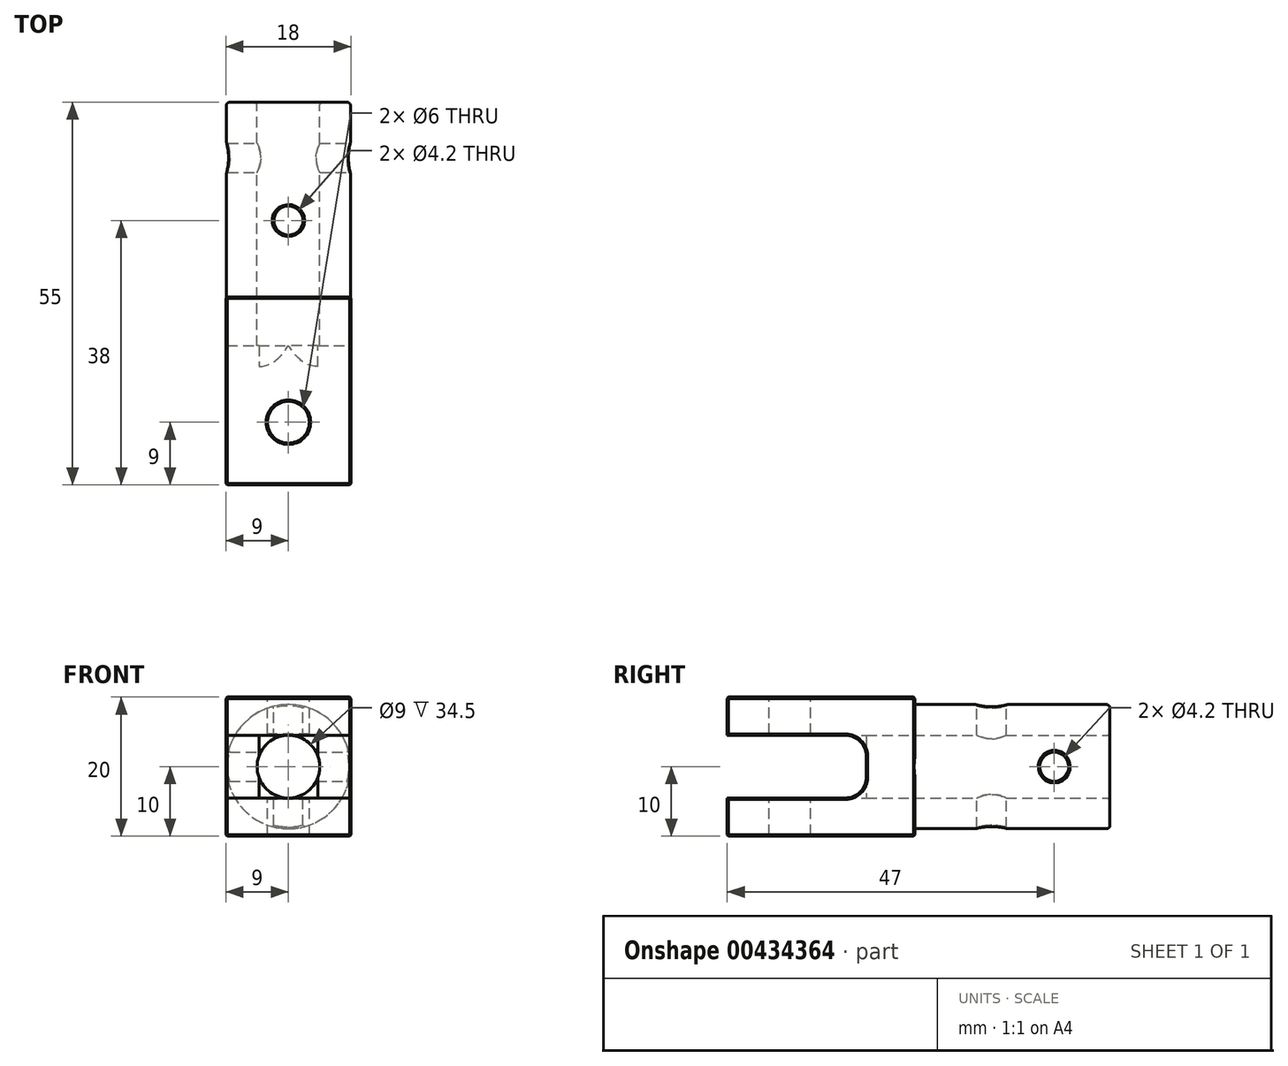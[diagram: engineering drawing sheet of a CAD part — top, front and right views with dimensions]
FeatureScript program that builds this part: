
annotation { "Feature Type Name" : "Feature", "Feature Type Description" : "" }
export const myFeature = defineFeature(function(context is Context, id is Id, definition is map)
    precondition{}
    {
        {
            var Q0;
            Q0=qCreatedBy(makeId("Front.planeOp"),FACE);
            var sketch = newSketch(context, id + "F0", { "sketchPlane" : qUnion([Q0])});
            skLineSegment(sketch, "E0.bottom", {"start": v(-9, 10) * mm, "end": v(9, 10) * mm});
            skLineSegment(sketch, "E0.top", {"start": v(-9, -10) * mm, "end": v(9, -10) * mm});
            skLineSegment(sketch, "E0.left", {"start": v(-9, 10) * mm, "end": v(-9, -10) * mm});
            skLineSegment(sketch, "E0.right", {"start": v(9, 10) * mm, "end": v(9, -10) * mm});
            skPoint(sketch, "E0.middle", {"position": v(0, 0) * mm});
            skCircle(sketch, "E1", {"center": v(0, 0) * mm, "radius": 4.5 * mm});
            skSolve(sketch);
        }
        {
            var Q0;
            Q0=makeQuery(id+"F0.imprint","IMPRINT",FACE,{"disambiguationData":[TD([[makeQuery(id+"F0.imprint","IMPRINT",EDGE,{"derivedFrom":sQuery(id+"F0.wireOp",EDGE,"E0.bottom")}),-1.0]])]});
            extrude(context, id + "F1", {"entities" : qUnion([Q0]), "depth" : 27 * mm, "offsetDistance" : 25 * mm});
        }
        {
            var Q0;
            Q0=qCreatedBy(makeId("Front.planeOp"),FACE);
            var sketch = newSketch(context, id + "F2", { "sketchPlane" : qUnion([Q0])});
            skCircle(sketch, "E2", {"center": v(0, 0) * mm, "radius": 8.93 * mm});
            skSolve(sketch);
        }
        {
            var Q0;
            Q0=makeQuery(id+"F2.imprint","IMPRINT",FACE,{"disambiguationData":[TD([[makeQuery(id+"F2.imprint","IMPRINT",EDGE,{"derivedFrom":sQuery(id+"F2.wireOp",EDGE,"E2")}),1.0]])]});
            extrude(context, id + "F3", {"entities" : qUnion([Q0]), "operationType" : NewBodyOperationType.ADD, "oppositeDirection" : true, "depth" : 28 * mm, "offsetDistance" : 25 * mm});
        }
        {
            var Q0;
            Q0=qCreatedBy(makeId("Front.planeOp"),FACE);
            var sketch = newSketch(context, id + "F4", { "sketchPlane" : qUnion([Q0])});
            skCircle(sketch, "E3", {"center": v(0, 0) * mm, "radius": 4.5 * mm});
            skSolve(sketch);
        }
        {
            var Q0;
            Q0=makeQuery(id+"F4.imprint","IMPRINT",FACE,{"disambiguationData":[TD([[makeQuery(id+"F4.imprint","IMPRINT",EDGE,{"derivedFrom":sQuery(id+"F4.wireOp",EDGE,"E3")}),1.0]])]});
            extrude(context, id + "F5", {"entities" : qUnion([Q0]), "operationType" : NewBodyOperationType.REMOVE, "endBound" : BoundingType.THROUGH_ALL, "oppositeDirection" : true, "depth" : 25 * mm, "offsetDistance" : 25 * mm});
        }
        {
            var Q0;
            Q0=makeQuery(id+"F1.opExtrude","CAP_FACE",FACE,{"disambiguationData":[OSD([sQuery(id+"F0.wireOp",EDGE,"E0.bottom"),sQuery(id+"F0.wireOp",EDGE,"E0.top"),sQuery(id+"F0.wireOp",EDGE,"E0.left"),sQuery(id+"F0.wireOp",EDGE,"E0.right"),sQuery(id+"F0.wireOp",EDGE,"E1")])],"isStart":false});
            var sketch = newSketch(context, id + "F6", { "sketchPlane" : qUnion([Q0])});
            skLineSegment(sketch, "E4.bottom", {"start": v(-9, 4.5) * mm, "end": v(9, 4.5) * mm});
            skLineSegment(sketch, "E4.top", {"start": v(-9, -4.5) * mm, "end": v(9, -4.5) * mm});
            skLineSegment(sketch, "E4.left", {"start": v(-9, 4.5) * mm, "end": v(-9, -4.5) * mm});
            skLineSegment(sketch, "E4.right", {"start": v(9, 4.5) * mm, "end": v(9, -4.5) * mm});
            skPoint(sketch, "E5.endSnap0", {"position": v(9, 0) * mm});
            skSolve(sketch);
        }
        {
            var Q0;
            {var subQ0=sQuery(id+"F6.wireOp",EDGE,"E4.left");Q0=makeQuery(id+"F6.imprint","IMPRINT",FACE,{"disambiguationData":[TD([[makeQuery(id+"F6.imprint","IMPRINT",EDGE,{"derivedFrom":subQ0}),1.0]])]});}
            var Q1;
            {var subQ0=sQuery(id+"F6.wireOp",EDGE,"E4.right");Q1=makeQuery(id+"F6.imprint","IMPRINT",FACE,{"disambiguationData":[TD([[makeQuery(id+"F6.imprint","IMPRINT",EDGE,{"derivedFrom":subQ0}),-1.0]])]});}
            extrude(context, id + "F7", {"entities" : qUnion([Q0, Q1]), "operationType" : NewBodyOperationType.REMOVE, "oppositeDirection" : true, "depth" : 20 * mm, "offsetDistance" : 25 * mm});
        }
        {
            var Q0;
            {var subQ0=sQuery(id+"F6.wireOp",EDGE,"E4.bottom");Q0=makeQuery(id+"F7.boolean.opBoolean","COPY",EDGE,{"derivedFrom":makeQuery(id+"F7.opExtrude","CAP_EDGE",EDGE,{"disambiguationData":[OSD([subQ0]),TDD([makeQuery(id+"F6.imprint","IMPRINT",EDGE,{"disambiguationData":[TD([[makeQuery(id+"F6.imprint","INTERSECT",VERTEX,{"derivedFrom":[makeQuery(id+"F1.opExtrude","CAP_EDGE",EDGE,{"disambiguationData":[OSD([sQuery(id+"F0.wireOp",EDGE,"E1")])],"isStart":false}),subQ0]}),-1.0]])],"derivedFrom":subQ0})])],"isStart":false})});}
            var Q1;
            {var subQ0=sQuery(id+"F6.wireOp",EDGE,"E4.top");Q1=makeQuery(id+"F7.boolean.opBoolean","COPY",EDGE,{"derivedFrom":makeQuery(id+"F7.opExtrude","CAP_EDGE",EDGE,{"disambiguationData":[OSD([subQ0]),TDD([makeQuery(id+"F6.imprint","IMPRINT",EDGE,{"disambiguationData":[TD([[makeQuery(id+"F6.imprint","INTERSECT",VERTEX,{"derivedFrom":[makeQuery(id+"F1.opExtrude","CAP_EDGE",EDGE,{"disambiguationData":[OSD([sQuery(id+"F0.wireOp",EDGE,"E1")])],"isStart":false}),subQ0]}),-1.0]])],"derivedFrom":subQ0})])],"isStart":false})});}
            fillet(context, id + "F8", {"entities" : qUnion([Q0, Q1]), "tangentPropagation" : true, "radius" : 3 * mm, "defaultsChanged" : false, "vertexSettings" : [], "allowEdgeOverflow" : false});
        }
        {
            var Q0;
            Q0=makeQuery(id+"F3.opExtrude","CAP_EDGE",EDGE,{"disambiguationData":[OSD([sQuery(id+"F2.wireOp",EDGE,"E2")])],"isStart":true});
            var Q1;
            Q1=makeQuery(id+"F3.opExtrude","CAP_EDGE",EDGE,{"disambiguationData":[OSD([sQuery(id+"F2.wireOp",EDGE,"E2")])],"isStart":false});
            var Q2;
            Q2=makeQuery(id+"F5.boolean.opBoolean","INTERSECT",EDGE,{"derivedFrom":[makeQuery(id+"F3.opExtrude","CAP_FACE",FACE,{"disambiguationData":[OSD([sQuery(id+"F2.wireOp",EDGE,"E2")])],"isStart":false}),makeQuery(id+"F5.opExtrude","SWEPT_FACE",FACE,{"disambiguationData":[OSD([sQuery(id+"F4.wireOp",EDGE,"E3")])]})]});
            fillet(context, id + "F9", {"entities" : qUnion([Q0, Q1, Q2]), "tangentPropagation" : true, "radius" : 0.5 * mm, "defaultsChanged" : false, "vertexSettings" : [], "allowEdgeOverflow" : false});
        }
        {
            var Q0;
            Q0=makeQuery(id+"F1.opExtrude","SWEPT_FACE",FACE,{"disambiguationData":[OSD([sQuery(id+"F0.wireOp",EDGE,"E0.bottom")])]});
            var sketch = newSketch(context, id + "F10", { "sketchPlane" : qUnion([Q0])});
            skCircle(sketch, "E6", {"center": v(0, -18) * mm, "radius": 3 * mm});
            skSolve(sketch);
        }
        {
            var Q0;
            Q0=makeQuery(id+"F10.imprint","IMPRINT",FACE,{"disambiguationData":[TD([[makeQuery(id+"F10.imprint","IMPRINT",EDGE,{"derivedFrom":sQuery(id+"F10.wireOp",EDGE,"E6")}),1.0]])]});
            var Q1;
            Q1=sQuery(id+"F10.wireOp",EDGE,"E6");
            extrude(context, id + "F11", {"entities" : qUnion([Q0]), "operationType" : NewBodyOperationType.REMOVE, "surfaceEntities" : qUnion([Q1]), "oppositeDirection" : true, "depth" : 25 * mm, "offsetDistance" : 25 * mm});
        }
        {
            var Q0;
            Q0=makeQuery(id+"F1.opExtrude","SWEPT_FACE",FACE,{"disambiguationData":[OSD([sQuery(id+"F0.wireOp",EDGE,"E0.bottom")])]});
            var sketch = newSketch(context, id + "F12", { "sketchPlane" : qUnion([Q0])});
            skCircle(sketch, "E7", {"center": v(0, 11) * mm, "radius": 2.1 * mm});
            skSolve(sketch);
        }
        {
            var Q0;
            Q0=makeQuery(id+"F12.imprint","IMPRINT",FACE,{"disambiguationData":[TD([[makeQuery(id+"F12.imprint","IMPRINT",EDGE,{"derivedFrom":sQuery(id+"F12.wireOp",EDGE,"E7")}),1.0]])]});
            extrude(context, id + "F13", {"entities" : qUnion([Q0]), "operationType" : NewBodyOperationType.REMOVE, "oppositeDirection" : true, "depth" : 40 * mm, "offsetDistance" : 25 * mm, "symmetric" : true});
        }
        {
            var Q0;
            Q0=qCreatedBy(makeId("Right.planeOp"),FACE);
            var sketch = newSketch(context, id + "F14", { "sketchPlane" : qUnion([Q0])});
            skCircle(sketch, "E8", {"center": v(20, 0) * mm, "radius": 2.1 * mm});
            skSolve(sketch);
        }
        {
            var Q0;
            Q0=makeQuery(id+"F14.imprint","IMPRINT",FACE,{"disambiguationData":[TD([[makeQuery(id+"F14.imprint","IMPRINT",EDGE,{"derivedFrom":sQuery(id+"F14.wireOp",EDGE,"E8")}),1.0]])]});
            extrude(context, id + "F15", {"entities" : qUnion([Q0]), "operationType" : NewBodyOperationType.REMOVE, "oppositeDirection" : true, "depth" : 25 * mm, "offsetDistance" : 25 * mm, "symmetric" : true});
        }
        {
            var Q0;
            Q0=makeQuery(id+"F13.boolean.opBoolean","INTERSECT",EDGE,{"disambiguationData":[OD(0.0)],"derivedFrom":[makeQuery(id+"F3.opExtrude","SWEPT_FACE",FACE,{"disambiguationData":[OSD([sQuery(id+"F2.wireOp",EDGE,"E2")])]}),makeQuery(id+"F13.opExtrude","SWEPT_FACE",FACE,{"disambiguationData":[OSD([sQuery(id+"F12.wireOp",EDGE,"E7")])]})]});
            var Q1;
            Q1=makeQuery(id+"F15.boolean.opBoolean","INTERSECT",EDGE,{"disambiguationData":[OD(1.0)],"derivedFrom":[makeQuery(id+"F3.opExtrude","SWEPT_FACE",FACE,{"disambiguationData":[OSD([sQuery(id+"F2.wireOp",EDGE,"E2")])]}),makeQuery(id+"F15.opExtrude","SWEPT_FACE",FACE,{"disambiguationData":[OSD([sQuery(id+"F14.wireOp",EDGE,"E8")])]})]});
            var Q2;
            Q2=makeQuery(id+"F11.boolean.opBoolean","INTERSECT",EDGE,{"derivedFrom":[makeQuery(id+"F1.opExtrude","SWEPT_FACE",FACE,{"disambiguationData":[OSD([sQuery(id+"F0.wireOp",EDGE,"E0.top")])]}),makeQuery(id+"F11.opExtrude","SWEPT_FACE",FACE,{"disambiguationData":[OSD([sQuery(id+"F10.wireOp",EDGE,"E6")])]})]});
            var Q3;
            Q3=makeQuery(id+"F11.boolean.opBoolean","COPY",EDGE,{"derivedFrom":makeQuery(id+"F11.opExtrude","CAP_EDGE",EDGE,{"disambiguationData":[OSD([sQuery(id+"F10.wireOp",EDGE,"E6")])],"isStart":true})});
            var Q4;
            Q4=makeQuery(id+"F13.boolean.opBoolean","INTERSECT",EDGE,{"disambiguationData":[OD(1.0)],"derivedFrom":[makeQuery(id+"F3.opExtrude","SWEPT_FACE",FACE,{"disambiguationData":[OSD([sQuery(id+"F2.wireOp",EDGE,"E2")])]}),makeQuery(id+"F13.opExtrude","SWEPT_FACE",FACE,{"disambiguationData":[OSD([sQuery(id+"F12.wireOp",EDGE,"E7")])]})]});
            var Q5;
            Q5=makeQuery(id+"F15.boolean.opBoolean","INTERSECT",EDGE,{"disambiguationData":[OD(0.0)],"derivedFrom":[makeQuery(id+"F3.opExtrude","SWEPT_FACE",FACE,{"disambiguationData":[OSD([sQuery(id+"F2.wireOp",EDGE,"E2")])]}),makeQuery(id+"F15.opExtrude","SWEPT_FACE",FACE,{"disambiguationData":[OSD([sQuery(id+"F14.wireOp",EDGE,"E8")])]})]});
            var Q6;
            {var subQ0=sQuery(id+"F6.wireOp",EDGE,"E4.top");var subQ1=makeQuery(id+"F6.imprint","INTERSECT",VERTEX,{"derivedFrom":[makeQuery(id+"F1.opExtrude","CAP_EDGE",EDGE,{"disambiguationData":[OSD([sQuery(id+"F0.wireOp",EDGE,"E1")])],"isStart":false}),subQ0]});Q6=makeQuery(id+"F11.boolean.opBoolean","INTERSECT",EDGE,{"derivedFrom":[makeQuery(id+"F7.boolean.opBoolean","MERGE",FACE,{"derivedFrom":[],"fromTools":[makeQuery(id+"F7.opExtrude","SWEPT_FACE",FACE,{"disambiguationData":[OSD([subQ0]),TDD([makeQuery(id+"F6.imprint","IMPRINT",EDGE,{"disambiguationData":[TD([[subQ1,1.0]])],"derivedFrom":subQ0})])]}),makeQuery(id+"F7.opExtrude","SWEPT_FACE",FACE,{"disambiguationData":[OSD([subQ0]),TDD([makeQuery(id+"F6.imprint","IMPRINT",EDGE,{"disambiguationData":[TD([[subQ1,-1.0]])],"derivedFrom":subQ0})])]})]}),makeQuery(id+"F11.opExtrude","SWEPT_FACE",FACE,{"disambiguationData":[OSD([sQuery(id+"F10.wireOp",EDGE,"E6")])]})]});}
            var Q7;
            {var subQ0=sQuery(id+"F6.wireOp",EDGE,"E4.bottom");var subQ1=makeQuery(id+"F6.imprint","INTERSECT",VERTEX,{"derivedFrom":[makeQuery(id+"F1.opExtrude","CAP_EDGE",EDGE,{"disambiguationData":[OSD([sQuery(id+"F0.wireOp",EDGE,"E1")])],"isStart":false}),subQ0]});Q7=makeQuery(id+"F11.boolean.opBoolean","INTERSECT",EDGE,{"derivedFrom":[makeQuery(id+"F7.boolean.opBoolean","MERGE",FACE,{"derivedFrom":[],"fromTools":[makeQuery(id+"F7.opExtrude","SWEPT_FACE",FACE,{"disambiguationData":[OSD([subQ0]),TDD([makeQuery(id+"F6.imprint","IMPRINT",EDGE,{"disambiguationData":[TD([[subQ1,1.0]])],"derivedFrom":subQ0})])]}),makeQuery(id+"F7.opExtrude","SWEPT_FACE",FACE,{"disambiguationData":[OSD([subQ0]),TDD([makeQuery(id+"F6.imprint","IMPRINT",EDGE,{"disambiguationData":[TD([[subQ1,-1.0]])],"derivedFrom":subQ0})])]})]}),makeQuery(id+"F11.opExtrude","SWEPT_FACE",FACE,{"disambiguationData":[OSD([sQuery(id+"F10.wireOp",EDGE,"E6")])]})]});}
            var Q8;
            Q8=makeQuery(id+"F1.opExtrude","SWEPT_EDGE",EDGE,{"disambiguationData":[OSD([sQuery(id+"F0.wireOp",EDGE,"E0.bottom"),sQuery(id+"F0.wireOp",EDGE,"E0.right")])]});
            var Q9;
            Q9=makeQuery(id+"F1.opExtrude","CAP_EDGE",EDGE,{"disambiguationData":[OSD([sQuery(id+"F0.wireOp",EDGE,"E0.bottom")])],"isStart":true});
            var Q10;
            Q10=makeQuery(id+"F1.opExtrude","SWEPT_FACE",FACE,{"disambiguationData":[OSD([sQuery(id+"F0.wireOp",EDGE,"E0.bottom")])]});
            var Q11;
            Q11=makeQuery(id+"F1.opExtrude","SWEPT_FACE",FACE,{"disambiguationData":[OSD([sQuery(id+"F0.wireOp",EDGE,"E0.right")])]});
            var Q12;
            Q12=makeQuery(id+"F1.opExtrude","SWEPT_FACE",FACE,{"disambiguationData":[OSD([sQuery(id+"F0.wireOp",EDGE,"E0.top")])]});
            var Q13;
            Q13=makeQuery(id+"F1.opExtrude","SWEPT_FACE",FACE,{"disambiguationData":[OSD([sQuery(id+"F0.wireOp",EDGE,"E0.left")])]});
            chamfer(context, id + "F16", {"entities" : qUnion([Q0, Q1, Q2, Q3, Q4, Q5, Q6, Q7, Q8, Q9, Q10, Q11, Q12, Q13]), "width" : 0.2 * mm, "tangentPropagation" : true});
        }
    });
